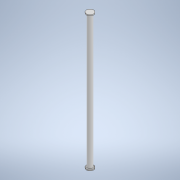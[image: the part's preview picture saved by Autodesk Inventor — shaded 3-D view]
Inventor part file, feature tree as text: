
AUTODESK INVENTOR PART (.ipt)
format: ipt  version: 2021 (Build 250183000, 183)  size: 101,376 bytes
history: native  units: in
note: dims shown in document units (in); Inventor stores cm internally (conversion verified against a paired STEP export)
features: extrude x2, mirror x2, sketch x2, projected_geometry x1
ambient origin geometry x8: Origin, YZ Plane, XZ Plane, XY Plane, X Axis, Y Axis, Z Axis, Center Point
bodies: Solid1 (feature_tree)
feature tree (7):
  extrude  "Extrusion1"  Depth=0.1in TaperAngle=0.0deg
  extrude  "Extrusion2"  Depth=7.0in TaperAngle=0.0deg
  mirror  "Mirror1"
  mirror  "Mirror2"
  sketch  "Sketch1"  dims[d0=0.75in d1=0.1in d2=0.0in]
  sketch  "Sketch2"  dims[d3=0.5in d4=7.0in d5=0.0in]
  projected_geometry  "Projected Loop1"
